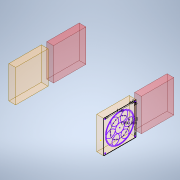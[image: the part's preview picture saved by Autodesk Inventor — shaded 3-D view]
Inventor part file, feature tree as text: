
AUTODESK INVENTOR PART (.ipt)
format: ipt  version: 2021.1 (Build 251245010, 245A)  size: 957,952 bytes
history: native  units: in
note: dims shown in document units (in); Inventor stores cm internally (conversion verified against a paired STEP export)
features: other x9, extrude x9, move_body x4, sketch x3, sheet_metal_op x1
ambient origin geometry x8: Origin, YZ Plane, XZ Plane, XY Plane, X Axis, Y Axis, Z Axis, Center Point
bodies: Body1 (feature_tree), Body2 (feature_tree), Body3 (feature_tree), Body4 (feature_tree), Body5 (feature_tree), Body6 (feature_tree)
feature tree (26):
  other  "bottom"
  sheet_metal_op  "face"
  extrude  "Extrusion9"  Depth=4.252in
  extrude  "Extrusion10"  Depth=4.1339in
  extrude  "Extrusion11"  Depth=4.7244in
  extrude  "Extrusion12"  Depth=0.9843in
  extrude  "Extrusion13"  Depth=4.7244in
  extrude  "Extrusion14"  Depth=0.315in
  extrude  "Extrusion15"  Depth=0.315in
  extrude  "Extrusion16"  Depth=0.1575in
  extrude  "Extrusion17"  Depth=13.7795in
  move_body  "Move Body1"
  move_body  "Move Body2"
  move_body  "Move Body3"
  move_body  "Move Body4"
  sketch  "Sketch6"  dims[d4=0.9843in d5=4.7244in d6=0.9843in d7=4.7244in d8=0.315in d9=0.315in d10=0.1575in d11=13.7795in d12=0.5906in d13=0.5906in d30=11.811in d31=0.0in d32=4.7244in d33=0.0in d34=4.1339in d35=0.0in d36=9.7638in d37=0.0in d38=0.5487in d39=0.0in d40=0.3612in d41=0.0in d42=11.811in d43=0.0in d45=0.315in d46=3.1496in d48=0.4724in d49=2.3622in d51=0.4724in d54=1.1265in d55=0.0in d57=3.1496in d59=2.3622in d60=0.315in d61=0.4724in d62=0.4724in d63=0.811in d64=0.0in d65=0.0in d66=0.0in d67=-0.3937in d68=0.0in d69=0.0in d70=-0.3937in d71=0.0in d72=0.0in d73=-0.3937in d74=0.0in d75=0.0in d76=-5.5118in d77=2.3622in d79=360.0deg d81=0.1575in d82=0.7874in d84=4.3307in d85=0.7874in d87=4.3307in]
  other  "fans"
  other  "TV-BOX"
  other  "Projector"
  other  "top"
  sketch  "Sketch4"  dims[d0=9.7638in d1=4.252in]
  sketch  "Sketch5"  dims[d2=1.1024in d3=4.1339in]
  other  "Composite1"
  other  "Composite2"
  other  "Srf1"
  other  "Srf2"
